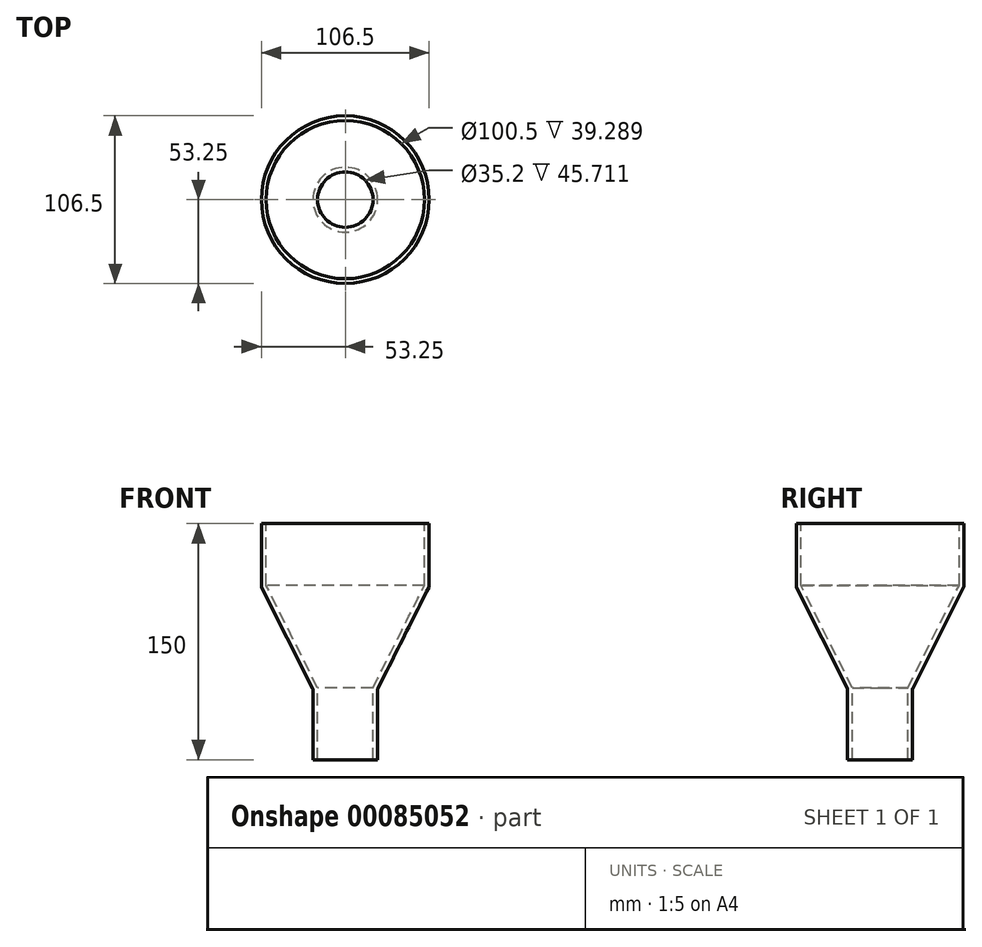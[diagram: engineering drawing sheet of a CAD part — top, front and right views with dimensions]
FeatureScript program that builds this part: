
annotation { "Feature Type Name" : "Feature", "Feature Type Description" : "" }
export const myFeature = defineFeature(function(context is Context, id is Id, definition is map)
    precondition{}
    {
        {
            var Q0;
            Q0=qCreatedBy(makeId("Front.planeOp"),FACE);
            var sketch = newSketch(context, id + "F0", { "sketchPlane" : qUnion([Q0])});
            skLineSegment(sketch, "E0", {"start": v(0, 98.88) * mm, "end": v(0, -76.03) * mm, "construction": true});
            skLineSegment(sketch, "E1", {"start": v(53.25, 75.56) * mm, "end": v(53.25, 35.56) * mm});
            skLineSegment(sketch, "E2", {"start": v(53.25, 35.56) * mm, "end": v(20.6, -29.44) * mm});
            skLineSegment(sketch, "E3", {"start": v(20.6, -29.44) * mm, "end": v(20.6, -74.44) * mm});
            skLineSegment(sketch, "E4.0", {"start": v(17.6, -28.73) * mm, "end": v(17.6, -74.44) * mm});
            skLineSegment(sketch, "E4.1", {"start": v(50.25, 36.27) * mm, "end": v(17.6, -28.73) * mm});
            skLineSegment(sketch, "E4.2", {"start": v(50.25, 75.56) * mm, "end": v(50.25, 36.27) * mm});
            skLineSegment(sketch, "E5", {"start": v(53.25, 75.56) * mm, "end": v(50.25, 75.56) * mm});
            skLineSegment(sketch, "E6", {"start": v(17.6, -74.44) * mm, "end": v(20.6, -74.44) * mm});
            skSolve(sketch);
        }
        {
            var Q0;
            Q0 = qSketchRegion(id + "F0", true);
            var Q1;
            Q1=sQuery(id+"F0.wireOp",EDGE,"E0");
            revolve(context, id + "F1", {"entities" : qUnion([Q0]), "axis" : qUnion([Q1]), "revolveType" : RevolveType.FULL});
        }
        {
            var Q0;
            Q0=makeQuery(id+"F1.opRevolve","SWEPT_EDGE",EDGE,{"disambiguationData":[OSD([sQuery(id+"F0.wireOp",EDGE,"E1"),sQuery(id+"F0.wireOp",EDGE,"E2")])]});
            var Q1;
            Q1=makeQuery(id+"F1.opRevolve","SWEPT_EDGE",EDGE,{"disambiguationData":[OSD([sQuery(id+"F0.wireOp",EDGE,"E2"),sQuery(id+"F0.wireOp",EDGE,"E3")])]});
            fillet(context, id + "F2", {"entities" : qUnion([Q0, Q1]), "radius" : 2 * mm, "tangentPropagation" : true, "allowEdgeOverflow" : false});
        }
    });
